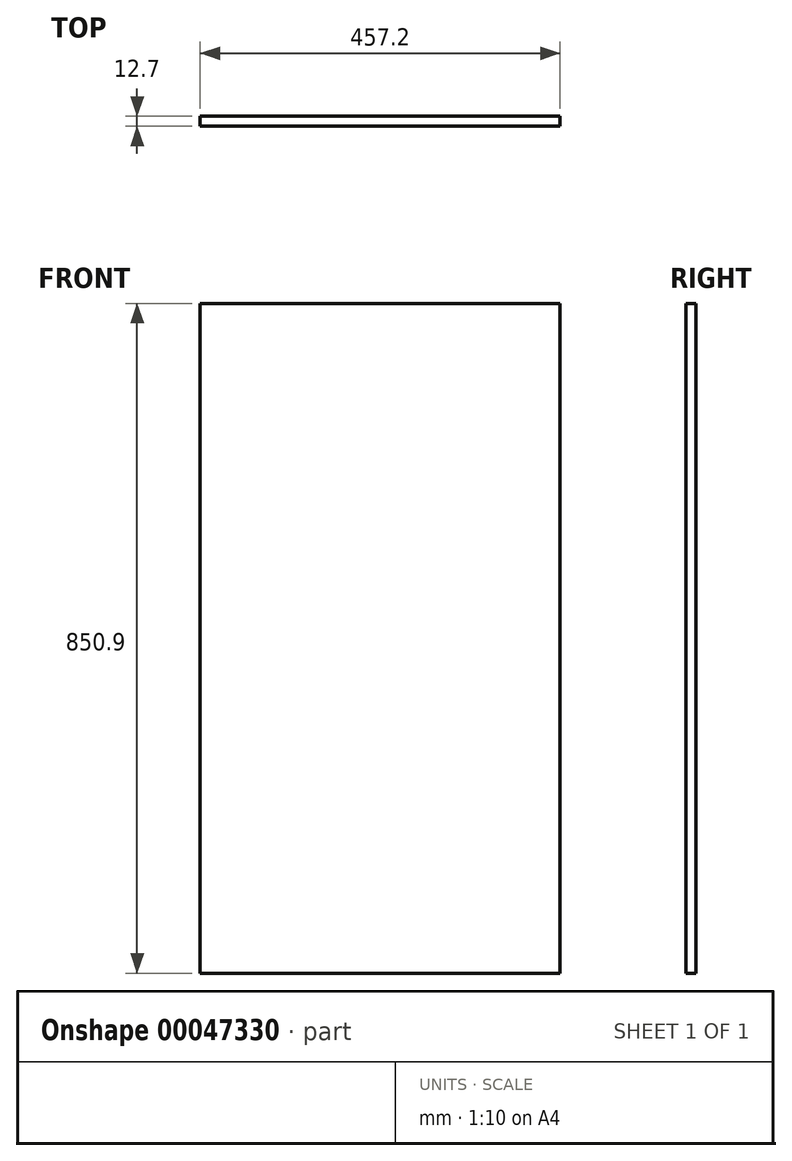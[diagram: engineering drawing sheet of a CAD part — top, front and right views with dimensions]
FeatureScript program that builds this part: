
annotation { "Feature Type Name" : "Feature", "Feature Type Description" : "" }
export const myFeature = defineFeature(function(context is Context, id is Id, definition is map)
    precondition{}
    {
        {
            var Q0;
            Q0=qCreatedBy(makeId("Front.planeOp"),FACE);
            var sketch = newSketch(context, id + "F0", { "sketchPlane" : qUnion([Q0])});
            skLineSegment(sketch, "E0.bottom", {"start": v(-28.08, 824.04) * mm, "end": v(429.12, 824.04) * mm});
            skLineSegment(sketch, "E0.top", {"start": v(-28.08, -26.86) * mm, "end": v(429.12, -26.86) * mm});
            skLineSegment(sketch, "E0.left", {"start": v(-28.08, 824.04) * mm, "end": v(-28.08, -26.86) * mm});
            skLineSegment(sketch, "E0.right", {"start": v(429.12, 824.04) * mm, "end": v(429.12, -26.86) * mm});
            skSolve(sketch);
        }
        {
            var Q0;
            Q0=makeQuery(id+"F0.imprint","IMPRINT",FACE,{"disambiguationData":[TD([[makeQuery(id+"F0.imprint","IMPRINT",EDGE,{"derivedFrom":sQuery(id+"F0.wireOp",EDGE,"E0.bottom")}),-1.0]])]});
            extrude(context, id + "F1", {"entities" : qUnion([Q0]), "depth" : 12.7 * mm});
        }
    });
